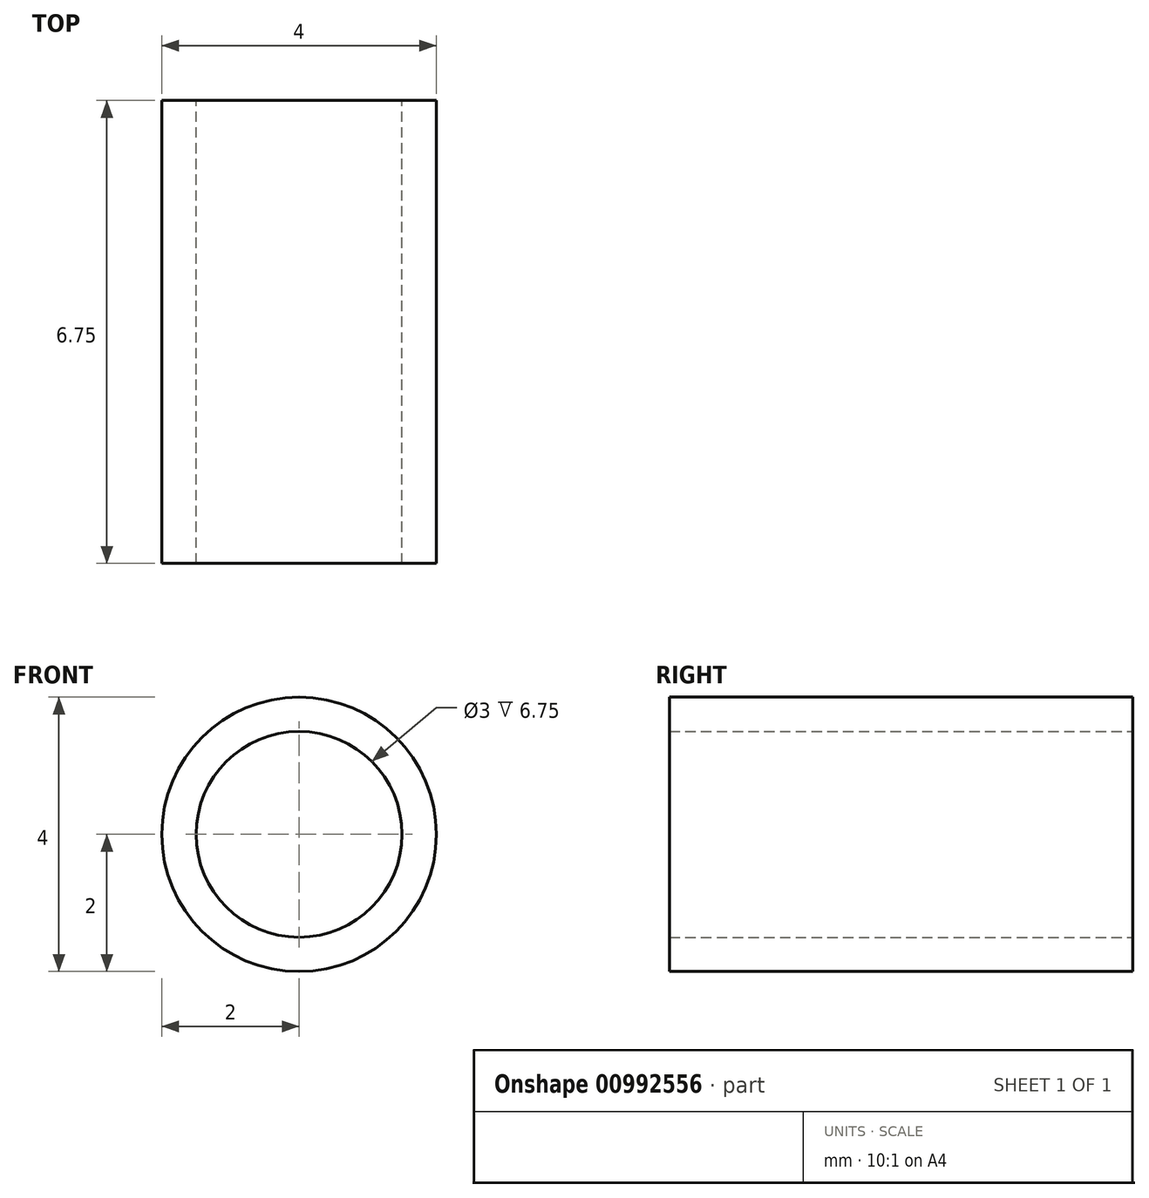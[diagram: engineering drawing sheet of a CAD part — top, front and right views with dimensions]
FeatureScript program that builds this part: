
annotation { "Feature Type Name" : "Feature", "Feature Type Description" : "" }
export const myFeature = defineFeature(function(context is Context, id is Id, definition is map)
    precondition{}
    {
        {
            var Q0;
            Q0=qCreatedBy(makeId("Front.planeOp"),FACE);
            var sketch = newSketch(context, id + "F0", { "sketchPlane" : qUnion([Q0])});
            skCircle(sketch, "E0", {"center": v(0, 0) * mm, "radius": 2 * mm});
            skCircle(sketch, "E1", {"center": v(0, 0) * mm, "radius": 1.5 * mm});
            skSolve(sketch);
        }
        {
            var Q0;
            Q0=qSketchRegion(id+"F0",true);
            extrude(context, id + "F1", {"entities" : qUnion([Q0]), "depth" : 6.75 * mm});
        }
    });
